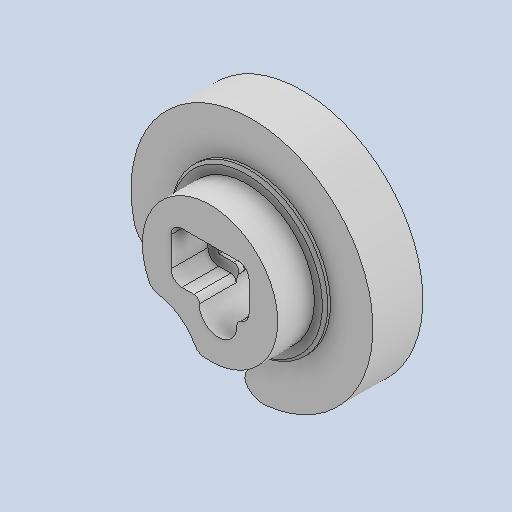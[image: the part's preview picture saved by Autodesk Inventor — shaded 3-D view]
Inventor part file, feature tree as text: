
AUTODESK INVENTOR PART (.ipt)
format: ipt  version: 2022 (Build 260153000, 153)  size: 313,344 bytes
history: native  units: mm
features: other x9, extrude x9, sketch x9, fillet x5, reference x5, projected_geometry x3, chamfer x1
ambient origin geometry x8: Origin, YZ Plane, XZ Plane, XY Plane, X Axis, Y Axis, Z Axis, Center Point
bodies: Body1 (feature_tree)
feature tree (41):
  other  "Твердое тело1"
  other  "РабПлоскость1"
  extrude  "Выдавливание1"  Depth=45.0mm
  extrude  "Выдавливание2"  Depth=10.0mm TaperAngle=0.0deg
  fillet  "Сопряжение1"  Radius=13.0mm
  extrude  "Выдавливание3"  Depth=3.0mm
  extrude  "Выдавливание4"  Depth=10.0mm TaperAngle=0.0deg
  fillet  "Сопряжение2"  Radius=4.0mm
  chamfer  "Фаска1"  Distance=25.2mm
  extrude  "Выдавливание5"  Depth=7.8mm TaperAngle=0.0deg
  extrude  "Выдавливание6"  Depth=2.0mm
  extrude  "Выдавливание7"  Depth=1.0mm TaperAngle=0.0deg
  extrude  "Выдавливание9"  Depth=2.0mm
  fillet  "Сопряжение3"  Radius=2.0mm
  fillet  "Сопряжение4"  Radius=4.2mm
  extrude  "Выдавливание10"  Depth=4.2mm
  fillet  "Сопряжение5"  Radius=4.2mm
  sketch  "Эскиз1"
  sketch  "Эскиз2"
  reference  "Ссылка1"
  sketch  "Эскиз3"
  sketch  "Эскиз4"
  projected_geometry  "Спроецированная петля1"
  projected_geometry  "Спроецированная петля2"
  sketch  "Эскиз5"
  reference  "Ссылка2"
  sketch  "Эскиз6"
  reference  "Ссылка3"
  sketch  "Эскиз7"
  reference  "Ссылка4"
  sketch  "Эскиз9"
  projected_geometry  "Спроецированная петля3"
  sketch  "Эскиз10"
  reference  "Ссылка5"
  other  "<userpath>\Documents\Git\MZCAT_2024\MZCAT.iam"
  other  "MZCAT.iam"
  other  "motor:2"
  other  "base plate:2"
  other  "<userpath>\Documents\Git\MZCAT_2024\MZCAT_4.iam"
  other  "MZCAT_4.iam"
  other  "base plate:1"
